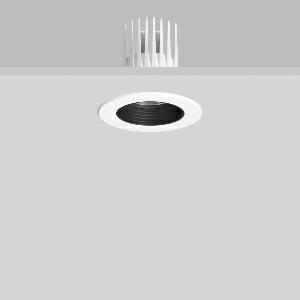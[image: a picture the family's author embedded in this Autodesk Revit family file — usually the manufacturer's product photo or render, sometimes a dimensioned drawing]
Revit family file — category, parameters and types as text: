
# Revit family: heledon_mini_e_901746_002_3_76_4e93
name_source: partatom
category: Lighting Fixtures
units: mm (PartAtom-declared; Revit-internal decimal feet)

## family parameters
Cut with Voids When Loaded = No
Host = Face
Light Source = No
Part Type = Normal
Room Calculation Point = No
Round Connector Dimension = Use Diameter
Shared = No

## types (1)
- HELEDON mini E (1 x LED Modul 935, 2300 lm, 3500)
    Apparent Load = 20 VA
    Approval mark = CE
    CIE Flux Codes = 80 99 100 100 100
    Color Rendering = 92
    Color Temperature = 3500
    Default Elevation = 1800 mm
    Description = Series: HELEDON mini
Round recessed downlight. Housing: die-cast aluminium, powder-coated. Black plastic ring and recessed LED to prevent glare from the side. Optical assembly with lens made of plastic (polycarbonate) for the best homogeneous light distribution - can be changed without tools. Best colour rendering index Ra>90. Suitable for Recessed ceiling mounting. Installation without tools thanks to spring fastening system. Including separate LED converter with connecting cable 600 mm.High quality converter without flickering and stroboscopic effect. Through-wiring box (5 pole) available as accessory. The following accessories can be mounted without use of tools: interchangeable lenses, decorative glasses, honeycomb louvre, clear and frosted diffusers, white interchangeable plastic ring. 
Colour: traffic white, matt (RAL 9016)
Diameter: 124 mm
Height: 3 mm
Cut-out diameter: 114 mm
Recess height: 170 mm
Luminaire: recess height: 120 mm
Lamp: LED
Socket: without socket
Colour temperature: 3500K
Colour rendering index (CRI): 92
System power: 20 W
Rated luminous flux: 2300 lm
Luminous efficiency: 115 lm/W
Control gear: Converter, dimmable, DALI
Protection class: II
Type of protection: IP 20
    Height = 0 mm  [stored 0 ft]
    Lamp = 1 x LED Modul 935
    Lamp Light Flux = 2300 lm
    Lamp count = 1
    Length = 124 mm  [stored 0.406824 ft]
    Lifetime = 50000 h
    Luminous efficacy = 115 lm/W
    Manufacturer = RZB
    ModVariant = No
    Model = 901746.002.3.76
    Mounting Place = Ceiling
    Mounting Type = Recessed
    Number of Poles = 1
    OnlyDefault = Yes
    Power Factor = 1
    Product Name = HELEDON mini E
    Product group = Recessed downlights
    ProductGroupID = 402
    Protection Class = Protection class II
    Protection Degree = IP 20
    RLX_Detail_Level = 1
    RLX_Emergency_Light_Flux = 0 lm
    RLX_Emergency_Type = 0
    RLX_Emergency_Type_DB = No
    RlxData = <blob elided: 126981 chars, md5=67a5cb19>
    Socket = socket
    Standby Power = 0 W
    System Light Flux = 2300 lm
    System Power = 20 W
    Type Comments = Product without accessories
    Type Image = 901656.002.jpg
    URL = http://relux.com
    VarID = ---
    Voltage = 230 V
    Voltage Range = 220-240 V
    Weight = 0.00 kg
    Width = 0 mm  [stored 0 ft]

note: [stored X ft] marks values corroborated as IEEE doubles in the binary element streams (Revit-internal decimal feet)

## geometry (parser evidence)
native form markers: Blend x4, Sweep x11
no freeform markers — native parametric forms only
